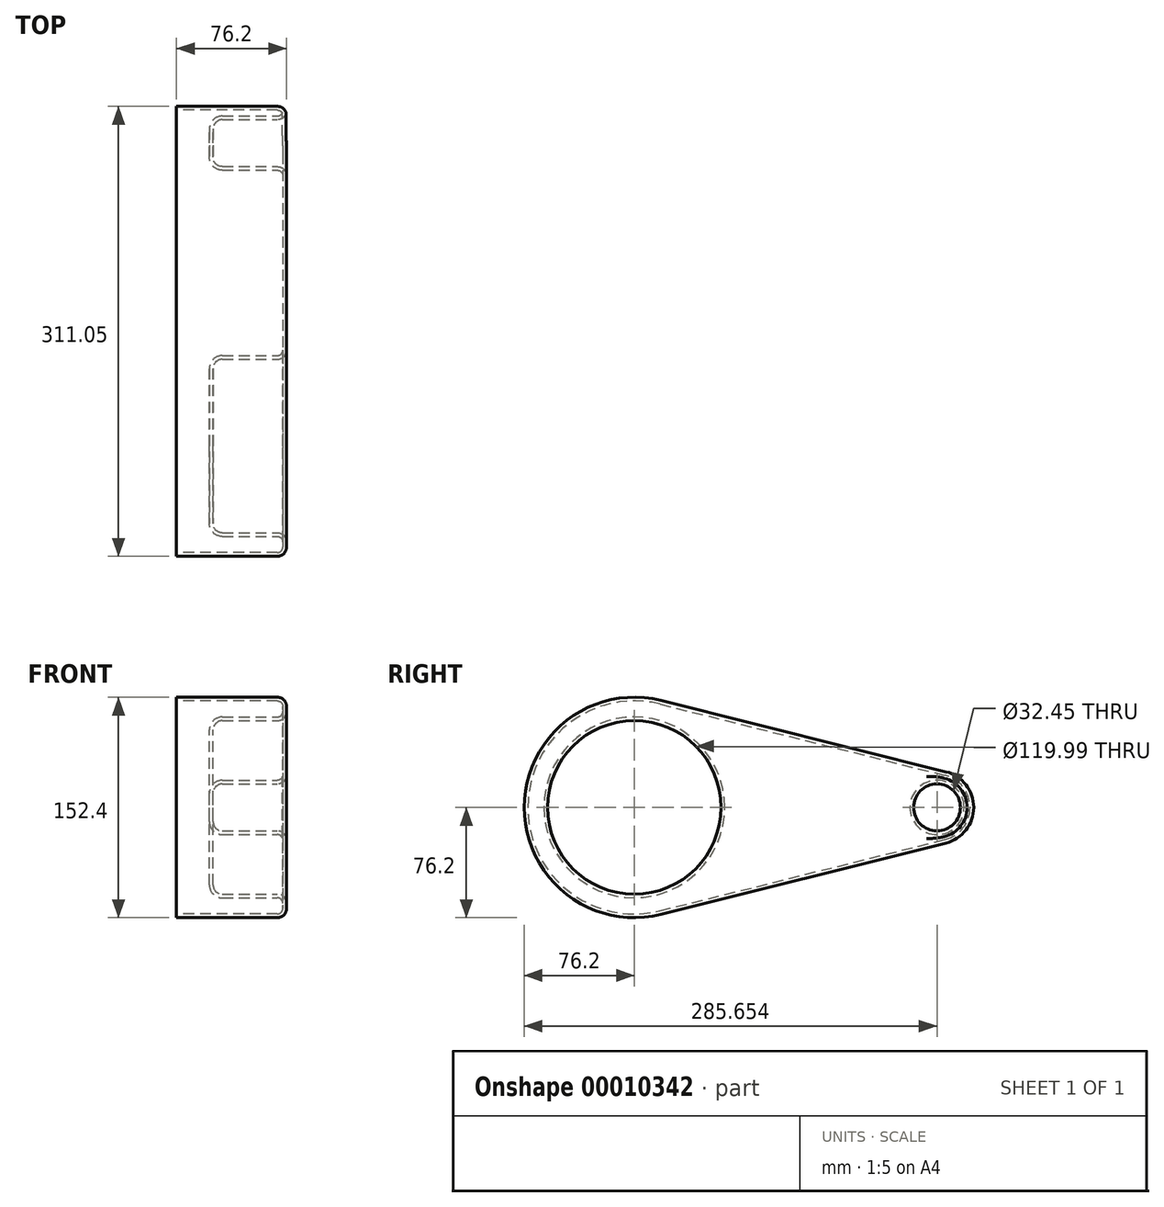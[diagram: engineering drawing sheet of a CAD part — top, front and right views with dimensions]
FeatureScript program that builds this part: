
annotation { "Feature Type Name" : "Feature", "Feature Type Description" : "" }
export const myFeature = defineFeature(function(context is Context, id is Id, definition is map)
    precondition{}
    {
        {
            var Q0;
            Q0=qCreatedBy(makeId("Right.planeOp"),FACE);
            var sketch = newSketch(context, id + "F0", { "sketchPlane" : qUnion([Q0])});
            skCircle(sketch, "E0", {"center": v(0, 0) * mm, "radius": 76.2 * mm});
            skCircle(sketch, "E1", {"center": v(209.45, 0) * mm, "radius": 25.4 * mm});
            skLineSegment(sketch, "E2", {"start": v(18.48, 73.92) * mm, "end": v(215.61, 24.64) * mm});
            skLineSegment(sketch, "E3", {"start": v(18.48, -73.92) * mm, "end": v(215.61, -24.64) * mm});
            skSolve(sketch);
        }
        {
            var Q0;
            {var subQ1=sQuery(id+"F0.wireOp",EDGE,"E2");Q0=makeQuery(id+"F0.imprint","IMPRINT",FACE,{"disambiguationData":[TD([[makeQuery(id+"F0.imprint","IMPRINT",EDGE,{"derivedFrom":subQ1}),-1.0]])]});}
            var Q1;
            Q1 = qSketchRegion(id + "F0", true);
            extrude(context, id + "F1", {"entities" : qUnion([Q0, Q1]), "depth" : 76.2 * mm});
        }
        {
            var Q0;
            Q0=makeQuery(id+"F1.opExtrude","CAP_FACE",FACE,{"disambiguationData":[OSD([sQuery(id+"F0.wireOp",EDGE,"E0"),sQuery(id+"F0.wireOp",EDGE,"E1"),sQuery(id+"F0.wireOp",EDGE,"E2"),sQuery(id+"F0.wireOp",EDGE,"E3")])],"isStart":false});
            var sketch = newSketch(context, id + "F2", { "sketchPlane" : qUnion([Q0])});
            skCircle(sketch, "E4", {"center": v(0, 0) * mm, "radius": 60 * mm});
            skCircle(sketch, "E5", {"center": v(209.45, 0) * mm, "radius": 16.23 * mm});
            skSolve(sketch);
        }
        {
            var Q0;
            Q0=makeQuery(id+"F2.imprint","IMPRINT",FACE,{"disambiguationData":[TD([[makeQuery(id+"F2.imprint","IMPRINT",EDGE,{"derivedFrom":sQuery(id+"F2.wireOp",EDGE,"E4")}),1.0]])]});
            var Q1;
            Q1=makeQuery(id+"F2.imprint","IMPRINT",FACE,{"disambiguationData":[TD([[makeQuery(id+"F2.imprint","IMPRINT",EDGE,{"derivedFrom":sQuery(id+"F2.wireOp",EDGE,"E5")}),1.0]])]});
            extrude(context, id + "F3", {"entities" : qUnion([Q0, Q1]), "operationType" : NewBodyOperationType.REMOVE, "oppositeDirection" : true, "depth" : 50.8 * mm});
        }
        {
            var Q0;
            Q0=makeQuery(id+"F1.opExtrude","CAP_FACE",FACE,{"disambiguationData":[OSD([sQuery(id+"F0.wireOp",EDGE,"E0"),sQuery(id+"F0.wireOp",EDGE,"E1"),sQuery(id+"F0.wireOp",EDGE,"E2"),sQuery(id+"F0.wireOp",EDGE,"E3")])],"isStart":false});
            var Q1;
            Q1=makeQuery(id+"F3.boolean.opBoolean","COPY",FACE,{"derivedFrom":makeQuery(id+"F3.opExtrude","CAP_FACE",FACE,{"disambiguationData":[OSD([sQuery(id+"F2.wireOp",EDGE,"E4")])],"isStart":false})});
            var Q2;
            Q2=makeQuery(id+"F3.boolean.opBoolean","COPY",FACE,{"derivedFrom":makeQuery(id+"F3.opExtrude","CAP_FACE",FACE,{"disambiguationData":[OSD([sQuery(id+"F2.wireOp",EDGE,"E5")])],"isStart":false})});
            fillet(context, id + "F4", {"entities" : qUnion([Q0, Q1, Q2]), "radius" : 6.35 * mm, "tangentPropagation" : true, "allowEdgeOverflow" : false});
        }
        {
            var Q0;
            Q0=makeQuery(id+"F1.opExtrude","CAP_FACE",FACE,{"disambiguationData":[OSD([sQuery(id+"F0.wireOp",EDGE,"E0"),sQuery(id+"F0.wireOp",EDGE,"E1"),sQuery(id+"F0.wireOp",EDGE,"E2"),sQuery(id+"F0.wireOp",EDGE,"E3")])],"isStart":true});
            shell(context, id + "F5", {"entities" : qUnion([Q0]), "thickness" : 2.54 * mm});
        }
    });
